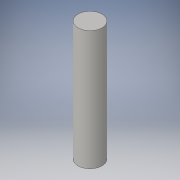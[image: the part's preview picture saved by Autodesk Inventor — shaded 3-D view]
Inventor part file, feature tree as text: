
AUTODESK INVENTOR PART (.ipt)
format: ipt  version: 2016 (Build 200138000, 138)  size: 83,968 bytes
history: native  units: in
note: dims shown in document units (in); Inventor stores cm internally (conversion verified against a paired STEP export)
features: extrude x1, sketch x1
ambient origin geometry x8: Origin, YZ Plane, XZ Plane, XY Plane, X Axis, Y Axis, Z Axis, Center Point
bodies: Solid1 (feature_tree)
feature tree (2):
  extrude  "Extrusion1"  Depth=1.25in TaperAngle=0.0deg
  sketch  "Sketch1"  dims[d0=0.25in d1=1.25in d2=0.0in]
